# Revit family: BE_84842_de_DE
name_source: partatom
category: Leuchten
units: mm (PartAtom-declared; Revit-internal decimal feet)

## family parameters
Basisbauteil = Fläche
Beim Laden mit Abzugskörper schneiden = Ja
Bemaßung runder Anschluss = Durchmesser verwenden
Gemeinsam genutzt = Nein
Lichtquelle = Ja
Raumberechnungspunkt = Ja
Teiletyp = Normal

## types (1)
- BEGA_84842_Grafit_K3
    AC/DC = AC
    Aktualisierung = 2022-05-19T04:00:07
    Anschlussleitung = 5.0 m X05RN-F FEP 2 × 1² + 1G2,5²
    Beschreibung = Gartenleuchte BEGA UniLink
    Beschreibung_Sonderanfertigung = Hier können Sie Informationen zur Sonderanfertigung eintragen.
    Bestellnummer = 84842K3
    CE_Konformität = ja
    Datei für fotometrisches Netz = BE_84842K3.IES
    Energieeffizienzklasse = LED A++ - A
    Farbfilter = 16777215
    Farbtemperatur = 3000 K
    Farbtemperaturverschiebung bei Dämpfen der Lampe = <Keine Auswahl>
    Farbwiedergabeindex = CRI > 80
    Frequenz = 50/60 Hz
    Gewicht = 2.0 kg
    Hersteller = BEGA
    LED_Modulbezeichnung = LED-1210/830
    Lampe = LED 3.8 W
    Lampenlichtstrom = 750 lm
    Lastklassifizierung = Beleuchtung
    Lebensdauerkriterien = L70B50 @ 25 °C = 180000 h
    Leuchtenlichtstrom = 537 lm
    Logo = BEGA_Logo.png
    M_A = Nein
    M_G = Ja
    M_W = Nein
    Material_03 = BEGA_Oberfläche_Weiss_matt
    Material_05 = BEGA_Oberfläche_Aluminium Guss
    Material_13 = BEGA_Kunststoff_matt
    Material_15 = BEGA_Leuchtmedium_matt
    Modell = 84842K3
    Neigungswinkel = 0.00°
    Produktdatenblatt = https://cdn.bega.com
    Scheinlast = 0 VA
    Schutzart = IP 65
    Schutzklasse = I
    Sonderanfertigung = Nein
    Spannung = 240 V
    Strom = 0,04 A
    URL = https://www.bega.com
    Umgebungstemperatur = 25 °C
    Vorgabe-Ansicht = 0 mm  [stored 0 ft]

note: [stored X ft] marks values corroborated as IEEE doubles in the binary element streams (Revit-internal decimal feet)
